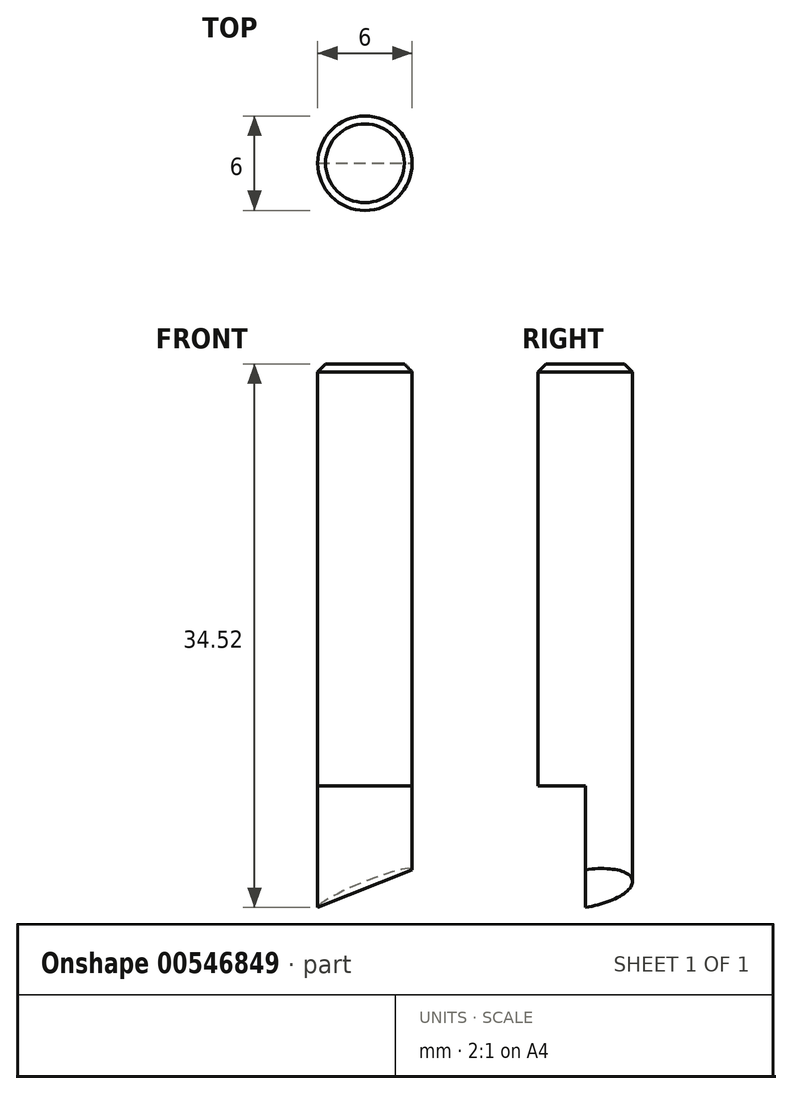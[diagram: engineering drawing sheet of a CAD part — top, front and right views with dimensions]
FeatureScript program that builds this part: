
annotation { "Feature Type Name" : "Feature", "Feature Type Description" : "" }
export const myFeature = defineFeature(function(context is Context, id is Id, definition is map)
    precondition{}
    {
        {
            var Q0;
            Q0=qCreatedBy(makeId("Top.planeOp"),FACE);
            var sketch = newSketch(context, id + "F0", { "sketchPlane" : qUnion([Q0])});
            skCircle(sketch, "E0", {"center": v(0, 0) * mm, "radius": 3 * mm});
            skSolve(sketch);
        }
        {
            var Q0;
            Q0=makeQuery(id+"F0.imprint","IMPRINT",FACE,{"disambiguationData":[TD([[makeQuery(id+"F0.imprint","IMPRINT",EDGE,{"derivedFrom":sQuery(id+"F0.wireOp",EDGE,"E0")}),1.0]])]});
            extrude(context, id + "F1", {"entities" : qUnion([Q0]), "depth" : 35 * mm, "offsetDistance" : 25 * mm});
        }
        {
            var Q0;
            Q0=makeQuery(id+"F1.opExtrude","CAP_EDGE",EDGE,{"disambiguationData":[OSD([sQuery(id+"F0.wireOp",EDGE,"E0")])],"isStart":false});
            chamfer(context, id + "F2", {"entities" : qUnion([Q0]), "width" : .5 * mm, "tangentPropagation" : true});
        }
        {
            var Q0;
            Q0=qCreatedBy(makeId("Right.planeOp"),FACE);
            var sketch = newSketch(context, id + "F3", { "sketchPlane" : qUnion([Q0])});
            skLineSegment(sketch, "E1.bottom", {"start": v(0, -17.28) * mm, "end": v(-14.16, -17.28) * mm});
            skLineSegment(sketch, "E1.top", {"start": v(0, 8.21) * mm, "end": v(-14.16, 8.21) * mm});
            skLineSegment(sketch, "E1.left", {"start": v(0, -17.28) * mm, "end": v(0, 8.21) * mm});
            skLineSegment(sketch, "E1.right", {"start": v(-14.16, -17.28) * mm, "end": v(-14.16, 8.21) * mm});
            skSolve(sketch);
        }
        {
            var Q0;
            Q0=makeQuery(id+"F3.imprint","IMPRINT",FACE,{"disambiguationData":[TD([[makeQuery(id+"F3.imprint","IMPRINT",EDGE,{"derivedFrom":sQuery(id+"F3.wireOp",EDGE,"E1.bottom")}),-1.0]])]});
            extrude(context, id + "F4", {"entities" : qUnion([Q0]), "operationType" : NewBodyOperationType.REMOVE, "oppositeDirection" : true, "depth" : 25 * mm, "offsetDistance" : 25 * mm, "hasSecondDirection" : true, "secondDirectionOppositeDirection" : false, "secondDirectionDepth" : 25 * mm});
        }
        {
            var Q0;
            Q0=qCreatedBy(makeId("Front.planeOp"),FACE);
            var sketch = newSketch(context, id + "F5", { "sketchPlane" : qUnion([Q0])});
            skLineSegment(sketch, "E2", {"start": v(30.6, 13.88) * mm, "end": v(30.6, -28.9) * mm});
            skLineSegment(sketch, "E3", {"start": v(30.6, -28.9) * mm, "end": v(-26.63, -10.48) * mm});
            skLineSegment(sketch, "E4", {"start": v(-26.63, -10.48) * mm, "end": v(-26.63, -8.95) * mm});
            skLineSegment(sketch, "E5", {"start": v(-26.63, -8.95) * mm, "end": v(30.6, 13.88) * mm});
            skSolve(sketch);
        }
        {
            var Q0;
            Q0=makeQuery(id+"F5.imprint","IMPRINT",FACE,{"disambiguationData":[TD([[makeQuery(id+"F5.imprint","IMPRINT",EDGE,{"derivedFrom":sQuery(id+"F5.wireOp",EDGE,"E2")}),-1.0]])]});
            extrude(context, id + "F6", {"entities" : qUnion([Q0]), "operationType" : NewBodyOperationType.REMOVE, "oppositeDirection" : true, "depth" : 25 * mm, "offsetDistance" : 25 * mm, "hasDraft" : true, "draftAngle" : 8 * degree});
        }
    });
